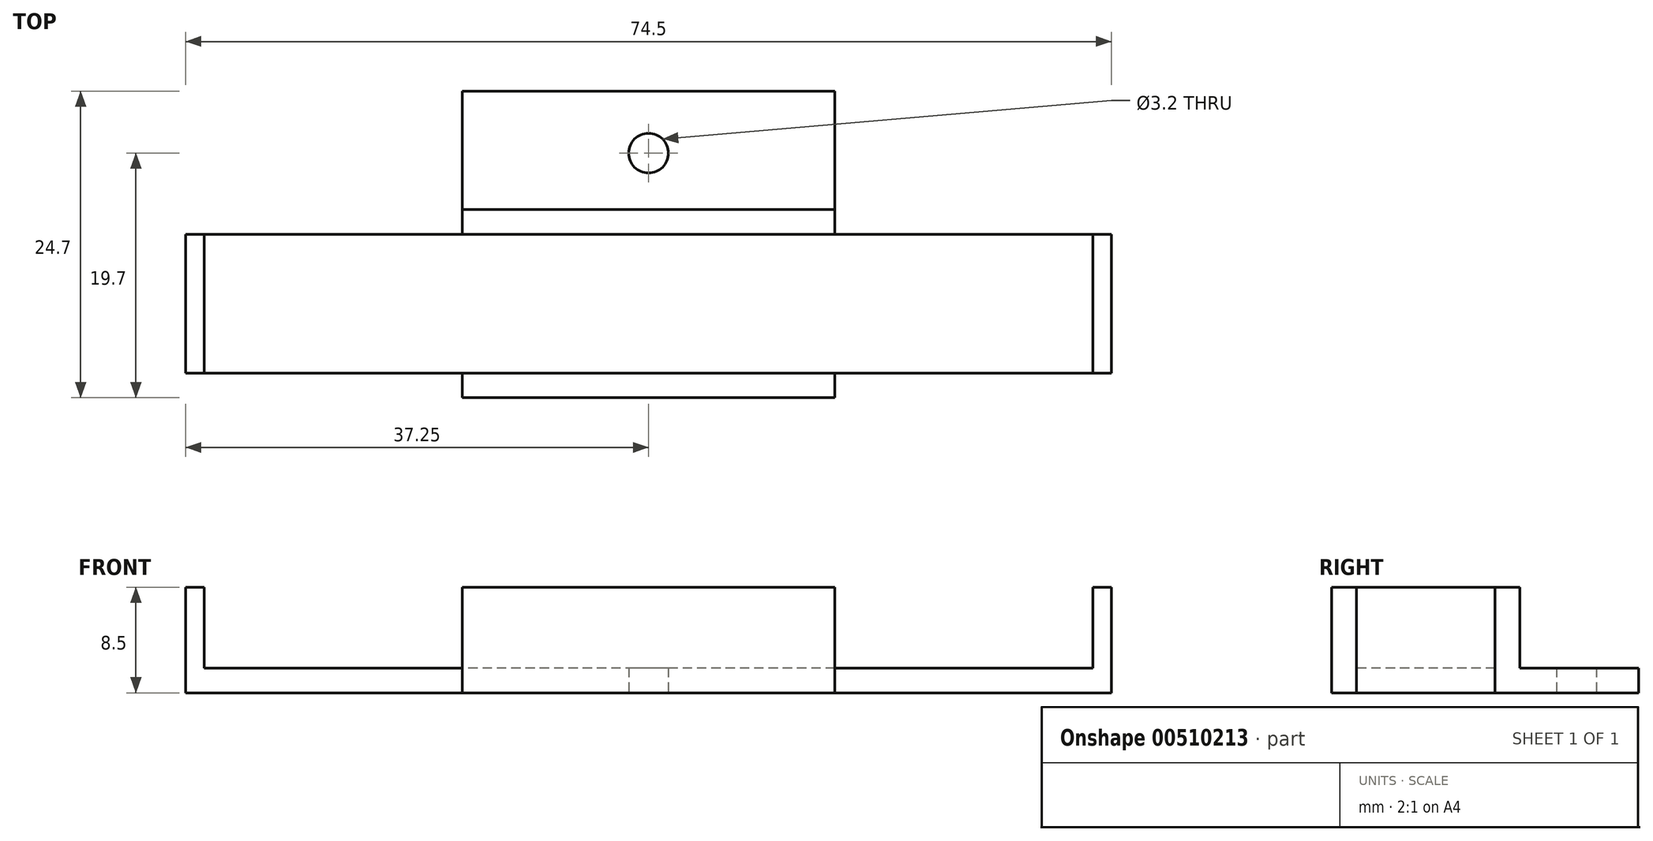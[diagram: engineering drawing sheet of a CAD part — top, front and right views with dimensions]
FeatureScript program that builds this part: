
annotation { "Feature Type Name" : "Feature", "Feature Type Description" : "" }
export const myFeature = defineFeature(function(context is Context, id is Id, definition is map)
    precondition{}
    {
        {
            var Q0;
            Q0=qCreatedBy(makeId("Top.planeOp"),FACE);
            var sketch = newSketch(context, id + "F0", { "sketchPlane" : qUnion([Q0])});
            skPoint(sketch, "E0", {"position": v(0, 17.7) * mm});
            skLineSegment(sketch, "E1.bottom", {"start": v(-15, 0) * mm, "end": v(15, 0) * mm});
            skLineSegment(sketch, "E1.top", {"start": v(-15, 11.15) * mm, "end": v(15, 11.15) * mm});
            skLineSegment(sketch, "E1.left", {"start": v(-15, 0) * mm, "end": v(-15, 11.15) * mm});
            skLineSegment(sketch, "E1.right", {"start": v(15, 0) * mm, "end": v(15, 11.15) * mm});
            skLineSegment(sketch, "E2.top", {"start": v(-15, 22.7) * mm, "end": v(15, 22.7) * mm});
            skLineSegment(sketch, "E2.left", {"start": v(-15, 11.15) * mm, "end": v(-15, 22.7) * mm});
            skLineSegment(sketch, "E2.right", {"start": v(15, 11.15) * mm, "end": v(15, 22.7) * mm});
            skLineSegment(sketch, "E3", {"start": v(-15, 13.15) * mm, "end": v(15, 13.15) * mm});
            skLineSegment(sketch, "E4.top", {"start": v(-15, -2) * mm, "end": v(15, -2) * mm});
            skLineSegment(sketch, "E4.left", {"start": v(-15, 0) * mm, "end": v(-15, -2) * mm});
            skLineSegment(sketch, "E4.right", {"start": v(15, 0) * mm, "end": v(15, -2) * mm});
            skLineSegment(sketch, "E5.bottom", {"start": v(-15, 11.15) * mm, "end": v(-35.75, 11.15) * mm});
            skLineSegment(sketch, "E5.top", {"start": v(-15, 0) * mm, "end": v(-35.75, 0) * mm});
            skLineSegment(sketch, "E5.left", {"start": v(-15, 11.15) * mm, "end": v(-15, 0) * mm});
            skLineSegment(sketch, "E5.right", {"start": v(-35.75, 11.15) * mm, "end": v(-35.75, 0) * mm});
            skLineSegment(sketch, "E6.bottom", {"start": v(15, 0) * mm, "end": v(35.75, 0) * mm});
            skLineSegment(sketch, "E6.top", {"start": v(15, 11.15) * mm, "end": v(35.75, 11.15) * mm});
            skLineSegment(sketch, "E6.right", {"start": v(35.75, 0) * mm, "end": v(35.75, 11.15) * mm});
            skLineSegment(sketch, "E7.bottom", {"start": v(-35.75, 0) * mm, "end": v(-37.25, 0) * mm});
            skLineSegment(sketch, "E7.top", {"start": v(-35.75, 11.15) * mm, "end": v(-37.25, 11.15) * mm});
            skLineSegment(sketch, "E7.left", {"start": v(-35.75, 0) * mm, "end": v(-35.75, 11.15) * mm});
            skLineSegment(sketch, "E7.right", {"start": v(-37.25, 0) * mm, "end": v(-37.25, 11.15) * mm});
            skLineSegment(sketch, "E8.bottom", {"start": v(35.75, 0) * mm, "end": v(37.25, 0) * mm});
            skLineSegment(sketch, "E8.top", {"start": v(35.75, 11.15) * mm, "end": v(37.25, 11.15) * mm});
            skLineSegment(sketch, "E8.right", {"start": v(37.25, 0) * mm, "end": v(37.25, 11.15) * mm});
            skSolve(sketch);
        }
        {
            var Q0;
            {var subQ0=sQuery(id+"F0.wireOp",EDGE,"E2.top");Q0=makeQuery(id+"F0.imprint","IMPRINT",FACE,{"disambiguationData":[TD([[makeQuery(id+"F0.imprint","IMPRINT",EDGE,{"derivedFrom":subQ0}),-1.0]])]});}
            var Q1;
            {var subQ0=sQuery(id+"F0.wireOp",EDGE,"E1.top");Q1=makeQuery(id+"F0.imprint","IMPRINT",FACE,{"disambiguationData":[TD([[makeQuery(id+"F0.imprint","IMPRINT",EDGE,{"derivedFrom":subQ0}),1.0]])]});}
            var Q2;
            Q2=makeQuery(id+"F0.imprint","IMPRINT",FACE,{"disambiguationData":[TD([[makeQuery(id+"F0.imprint","IMPRINT",EDGE,{"derivedFrom":sQuery(id+"F0.wireOp",EDGE,"E1.top")}),-1.0]])]});
            var Q3;
            Q3=makeQuery(id+"F0.imprint","IMPRINT",FACE,{"disambiguationData":[TD([[makeQuery(id+"F0.imprint","IMPRINT",EDGE,{"derivedFrom":sQuery(id+"F0.wireOp",EDGE,"E1.bottom")}),-1.0]])]});
            var Q4;
            Q4=makeQuery(id+"F0.imprint","IMPRINT",FACE,{"disambiguationData":[TD([[makeQuery(id+"F0.imprint","IMPRINT",EDGE,{"derivedFrom":sQuery(id+"F0.wireOp",EDGE,"E7.bottom")}),-1.0]])]});
            var Q5;
            Q5=makeQuery(id+"F0.imprint","IMPRINT",FACE,{"disambiguationData":[TD([[makeQuery(id+"F0.imprint","IMPRINT",EDGE,{"derivedFrom":sQuery(id+"F0.wireOp",EDGE,"E5.bottom")}),1.0]])]});
            var Q6;
            Q6=makeQuery(id+"F0.imprint","IMPRINT",FACE,{"disambiguationData":[TD([[makeQuery(id+"F0.imprint","IMPRINT",EDGE,{"derivedFrom":sQuery(id+"F0.wireOp",EDGE,"E6.bottom")}),1.0]])]});
            var Q7;
            Q7=makeQuery(id+"F0.imprint","IMPRINT",FACE,{"disambiguationData":[TD([[makeQuery(id+"F0.imprint","IMPRINT",EDGE,{"derivedFrom":sQuery(id+"F0.wireOp",EDGE,"E8.bottom")}),1.0]])]});
            extrude(context, id + "F1", {"entities" : qUnion([Q0, Q1, Q2, Q3, Q4, Q5, Q6, Q7]), "depth" : 2 * mm});
        }
        {
            var Q0;
            {var subQ0=sQuery(id+"F0.wireOp",EDGE,"E1.top");Q0=makeQuery(id+"F0.imprint","IMPRINT",FACE,{"disambiguationData":[TD([[makeQuery(id+"F0.imprint","IMPRINT",EDGE,{"derivedFrom":subQ0}),1.0]])]});}
            var Q1;
            Q1=makeQuery(id+"F0.imprint","IMPRINT",FACE,{"disambiguationData":[TD([[makeQuery(id+"F0.imprint","IMPRINT",EDGE,{"derivedFrom":sQuery(id+"F0.wireOp",EDGE,"E1.bottom")}),-1.0]])]});
            var Q2;
            Q2=makeQuery(id+"F0.imprint","IMPRINT",FACE,{"disambiguationData":[TD([[makeQuery(id+"F0.imprint","IMPRINT",EDGE,{"derivedFrom":sQuery(id+"F0.wireOp",EDGE,"E7.bottom")}),-1.0]])]});
            var Q3;
            Q3=makeQuery(id+"F0.imprint","IMPRINT",FACE,{"disambiguationData":[TD([[makeQuery(id+"F0.imprint","IMPRINT",EDGE,{"derivedFrom":sQuery(id+"F0.wireOp",EDGE,"E8.bottom")}),1.0]])]});
            extrude(context, id + "F2", {"entities" : qUnion([Q0, Q1, Q2, Q3]), "operationType" : NewBodyOperationType.ADD, "depth" : 8.5 * mm});
        }
        {
            var Q0;
            Q0=sQuery(id+"F0.wireOp",VERTEX,"E0");
            var Q1;
            Q1=makeQuery(id+"F1.opExtrude","SWEPT_BODY",BODY,{"disambiguationData":[OSD([sQuery(id+"F0.wireOp",EDGE,"E2.top"),sQuery(id+"F0.wireOp",EDGE,"E2.left"),sQuery(id+"F0.wireOp",EDGE,"E2.right"),sQuery(id+"F0.wireOp",EDGE,"E4.top"),sQuery(id+"F0.wireOp",EDGE,"E4.left"),sQuery(id+"F0.wireOp",EDGE,"E4.right"),sQuery(id+"F0.wireOp",EDGE,"E5.bottom"),sQuery(id+"F0.wireOp",EDGE,"E5.top"),sQuery(id+"F0.wireOp",EDGE,"E6.bottom"),sQuery(id+"F0.wireOp",EDGE,"E6.top"),sQuery(id+"F0.wireOp",EDGE,"E7.bottom"),sQuery(id+"F0.wireOp",EDGE,"E7.top"),sQuery(id+"F0.wireOp",EDGE,"E7.right"),sQuery(id+"F0.wireOp",EDGE,"E8.bottom"),sQuery(id+"F0.wireOp",EDGE,"E8.top"),sQuery(id+"F0.wireOp",EDGE,"E8.right")])]});
            hole(context, id + "F3", {"style" : HoleStyle.SIMPLE, "endStyle" : HoleEndStyle.THROUGH, "oppositeDirection" : true, "holeDiameter" : 3.2 * mm, "isTappedThrough" : true, "tappedDepth" : 12 * mm, "tapClearance" : 3, "startFromSketch" : true, "locations" : qUnion([Q0]), "scope" : qUnion([Q1])});
        }
    });
